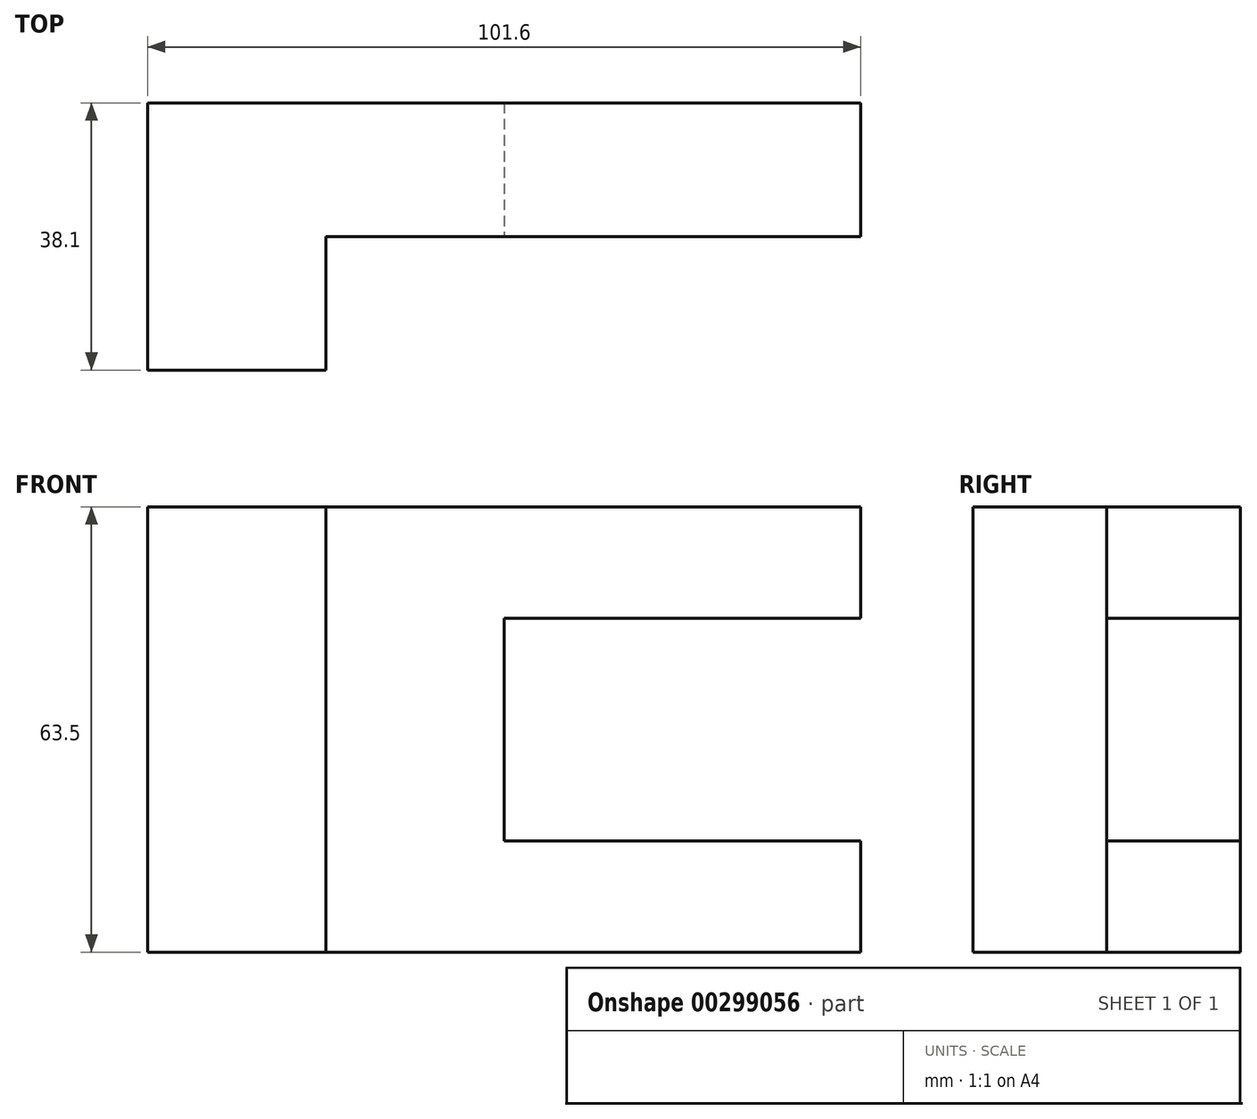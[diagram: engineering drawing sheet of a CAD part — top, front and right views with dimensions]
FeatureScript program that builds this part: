
annotation { "Feature Type Name" : "Feature", "Feature Type Description" : "" }
export const myFeature = defineFeature(function(context is Context, id is Id, definition is map)
    precondition{}
    {
        {
            var Q0;
            Q0=qCreatedBy(makeId("Front.planeOp"),FACE);
            var sketch = newSketch(context, id + "F0", { "sketchPlane" : qUnion([Q0])});
            skLineSegment(sketch, "E0.bottom", {"start": v(-50.8, 31.75) * mm, "end": v(50.8, 31.75) * mm});
            skLineSegment(sketch, "E0.top", {"start": v(-50.8, -31.75) * mm, "end": v(50.8, -31.75) * mm});
            skLineSegment(sketch, "E0.left", {"start": v(-50.8, 31.75) * mm, "end": v(-50.8, -31.75) * mm});
            skLineSegment(sketch, "E0.right", {"start": v(50.8, 31.75) * mm, "end": v(50.8, -31.75) * mm});
            skPoint(sketch, "E0.middle", {"position": v(0, 0) * mm});
            skSolve(sketch);
        }
        {
            var Q0;
            Q0 = qSketchRegion(id + "F0", true);
            extrude(context, id + "F1", {"entities" : qUnion([Q0]), "depth" : 19.05 * mm});
        }
        {
            var Q0;
            Q0=makeQuery(id+"F1.opExtrude","CAP_FACE",FACE,{"disambiguationData":[OSD([sQuery(id+"F0.wireOp",EDGE,"E0.bottom"),sQuery(id+"F0.wireOp",EDGE,"E0.top"),sQuery(id+"F0.wireOp",EDGE,"E0.left"),sQuery(id+"F0.wireOp",EDGE,"E0.right")])],"isStart":false});
            var sketch = newSketch(context, id + "F2", { "sketchPlane" : qUnion([Q0])});
            skLineSegment(sketch, "E1.bottom", {"start": v(-50.8, 31.75) * mm, "end": v(-25.4, 31.75) * mm});
            skLineSegment(sketch, "E1.top", {"start": v(-50.8, -31.75) * mm, "end": v(-25.4, -31.75) * mm});
            skLineSegment(sketch, "E1.left", {"start": v(-50.8, 31.75) * mm, "end": v(-50.8, -31.75) * mm});
            skLineSegment(sketch, "E1.right", {"start": v(-25.4, 31.75) * mm, "end": v(-25.4, -31.75) * mm});
            skSolve(sketch);
        }
        {
            var Q0;
            Q0 = qSketchRegion(id + "F2", true);
            extrude(context, id + "F3", {"entities" : qUnion([Q0]), "operationType" : NewBodyOperationType.ADD, "depth" : 19.05 * mm});
        }
        {
            var Q0;
            Q0=makeQuery(id+"F1.opExtrude","CAP_FACE",FACE,{"disambiguationData":[OSD([sQuery(id+"F0.wireOp",EDGE,"E0.bottom"),sQuery(id+"F0.wireOp",EDGE,"E0.top"),sQuery(id+"F0.wireOp",EDGE,"E0.left"),sQuery(id+"F0.wireOp",EDGE,"E0.right")])],"isStart":false});
            var sketch = newSketch(context, id + "F4", { "sketchPlane" : qUnion([Q0])});
            skLineSegment(sketch, "E2.bottom", {"start": v(50.8, -15.87) * mm, "end": v(0, -15.87) * mm});
            skLineSegment(sketch, "E2.top", {"start": v(50.8, 15.88) * mm, "end": v(0, 15.88) * mm});
            skLineSegment(sketch, "E2.left", {"start": v(50.8, -15.88) * mm, "end": v(50.8, 15.88) * mm});
            skLineSegment(sketch, "E2.right", {"start": v(0, -15.87) * mm, "end": v(0, 15.88) * mm});
            skPoint(sketch, "E2.middle", {"position": v(25.4, 0) * mm});
            skSolve(sketch);
        }
        {
            var Q0;
            Q0 = qSketchRegion(id + "F4", true);
            extrude(context, id + "F5", {"entities" : qUnion([Q0]), "operationType" : NewBodyOperationType.REMOVE, "oppositeDirection" : true, "depth" : 25.4 * mm});
        }
    });
